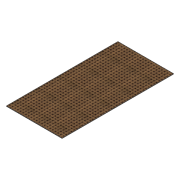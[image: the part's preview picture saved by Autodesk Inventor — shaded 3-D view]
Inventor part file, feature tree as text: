
AUTODESK INVENTOR PART (.ipt)
format: ipt  version: 2020.2 (Build 242310000, 310)  size: 109,056 bytes
history: native  units: mm
features: extrude x1, sketch x1
ambient origin geometry x8: Origin, YZ Plane, XZ Plane, XY Plane, X Axis, Y Axis, Z Axis, Center Point
bodies: Solid1 (feature_tree)
feature tree (2):
  extrude  "Extrusion1"  Depth=2000.0mm
  sketch  "Sketch1"  dims[d0=1000.0mm d1=2000.0mm d2=5.0mm d3=0.0mm]
